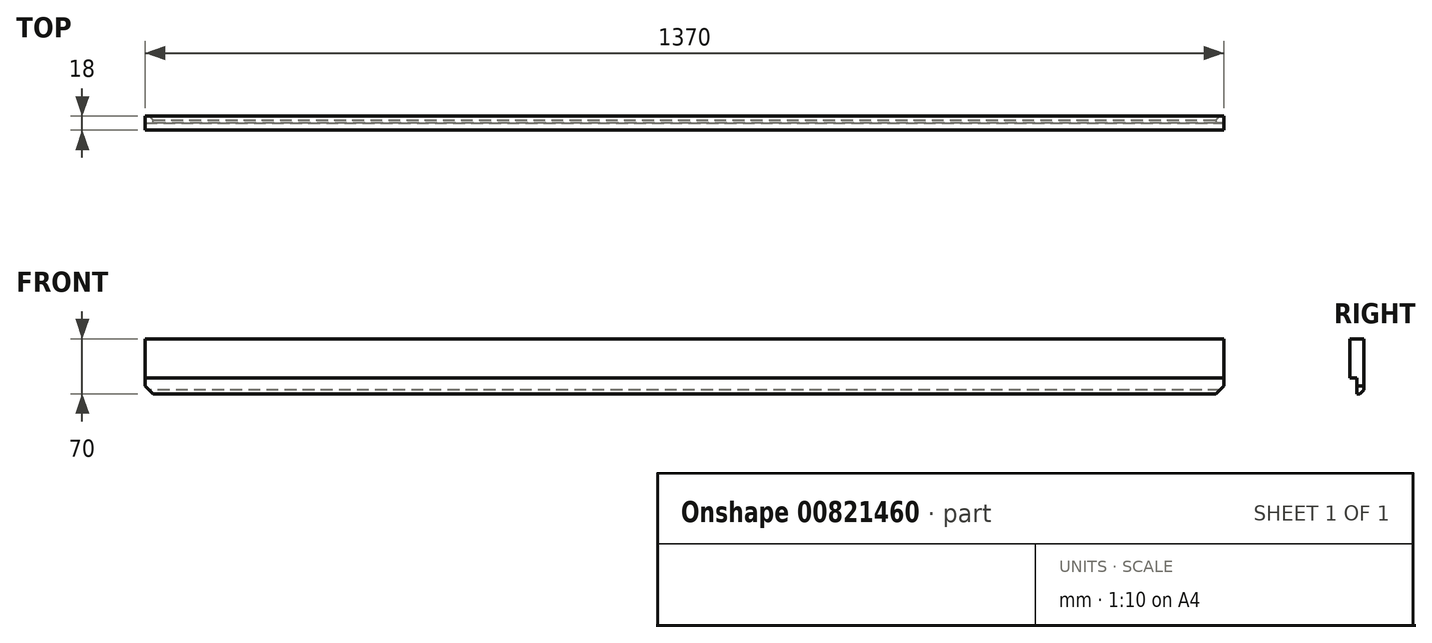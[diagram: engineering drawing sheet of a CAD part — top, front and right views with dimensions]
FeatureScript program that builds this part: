
annotation { "Feature Type Name" : "Feature", "Feature Type Description" : "" }
export const myFeature = defineFeature(function(context is Context, id is Id, definition is map)
    precondition{}
    {
        {
            var Q0;
            Q0=qCreatedBy(makeId("Front.planeOp"),FACE);
            var sketch = newSketch(context, id + "F0", { "sketchPlane" : qUnion([Q0])});
            skLineSegment(sketch, "E0.bottom", {"start": v(685, 35) * mm, "end": v(-685, 35) * mm});
            skLineSegment(sketch, "E0.top", {"start": v(685, -35) * mm, "end": v(-685, -35) * mm});
            skLineSegment(sketch, "E0.left", {"start": v(685, 35) * mm, "end": v(685, -35) * mm});
            skLineSegment(sketch, "E0.right", {"start": v(-685, 35) * mm, "end": v(-685, -35) * mm});
            skPoint(sketch, "E0.middle", {"position": v(0, 0) * mm});
            skSolve(sketch);
        }
        {
            var Q0;
            Q0=makeQuery(id+"F0.imprint","IMPRINT",FACE,{"disambiguationData":[TD([[makeQuery(id+"F0.imprint","IMPRINT",EDGE,{"derivedFrom":sQuery(id+"F0.wireOp",EDGE,"E0.bottom")}),1.0]])]});
            extrude(context, id + "F1", {"entities" : qUnion([Q0]), "depth" : 9 * mm, "offsetDistance" : 25 * mm});
        }
        {
            var Q0;
            Q0=makeQuery(id+"F1.opExtrude","CAP_FACE",FACE,{"disambiguationData":[OSD([sQuery(id+"F0.wireOp",EDGE,"E0.bottom"),sQuery(id+"F0.wireOp",EDGE,"E0.top"),sQuery(id+"F0.wireOp",EDGE,"E0.left"),sQuery(id+"F0.wireOp",EDGE,"E0.right")])],"isStart":false});
            var sketch = newSketch(context, id + "F2", { "sketchPlane" : qUnion([Q0])});
            skLineSegment(sketch, "E1.bottom", {"start": v(-685, 35) * mm, "end": v(685, 35) * mm});
            skLineSegment(sketch, "E1.top", {"start": v(-685, -15) * mm, "end": v(685, -15) * mm});
            skLineSegment(sketch, "E1.left", {"start": v(-685, 35) * mm, "end": v(-685, -15) * mm});
            skLineSegment(sketch, "E1.right", {"start": v(685, 35) * mm, "end": v(685, -15) * mm});
            skSolve(sketch);
        }
        {
            var Q0;
            Q0 = qSketchRegion(id + "F2", true);
            extrude(context, id + "F3", {"entities" : qUnion([Q0]), "operationType" : NewBodyOperationType.ADD, "depth" : 9 * mm, "offsetDistance" : 25 * mm});
        }
        {
            var Q0;
            Q0=makeQuery(id+"F1.opExtrude","SWEPT_EDGE",EDGE,{"disambiguationData":[OSD([sQuery(id+"F0.wireOp",EDGE,"E0.top"),sQuery(id+"F0.wireOp",EDGE,"E0.left")])]});
            var Q1;
            Q1=makeQuery(id+"F1.opExtrude","SWEPT_EDGE",EDGE,{"disambiguationData":[OSD([sQuery(id+"F0.wireOp",EDGE,"E0.top"),sQuery(id+"F0.wireOp",EDGE,"E0.right")])]});
            chamfer(context, id + "F4", {"entities" : qUnion([Q0, Q1]), "width" : 10 * mm, "tangentPropagation" : true});
        }
        {
            var Q0;
            Q0=makeQuery(id+"F1.opExtrude","CAP_EDGE",EDGE,{"disambiguationData":[OSD([sQuery(id+"F0.wireOp",EDGE,"E0.top")])],"isStart":true});
            chamfer(context, id + "F5", {"entities" : qUnion([Q0]), "width" : 5 * mm, "tangentPropagation" : true});
        }
    });
